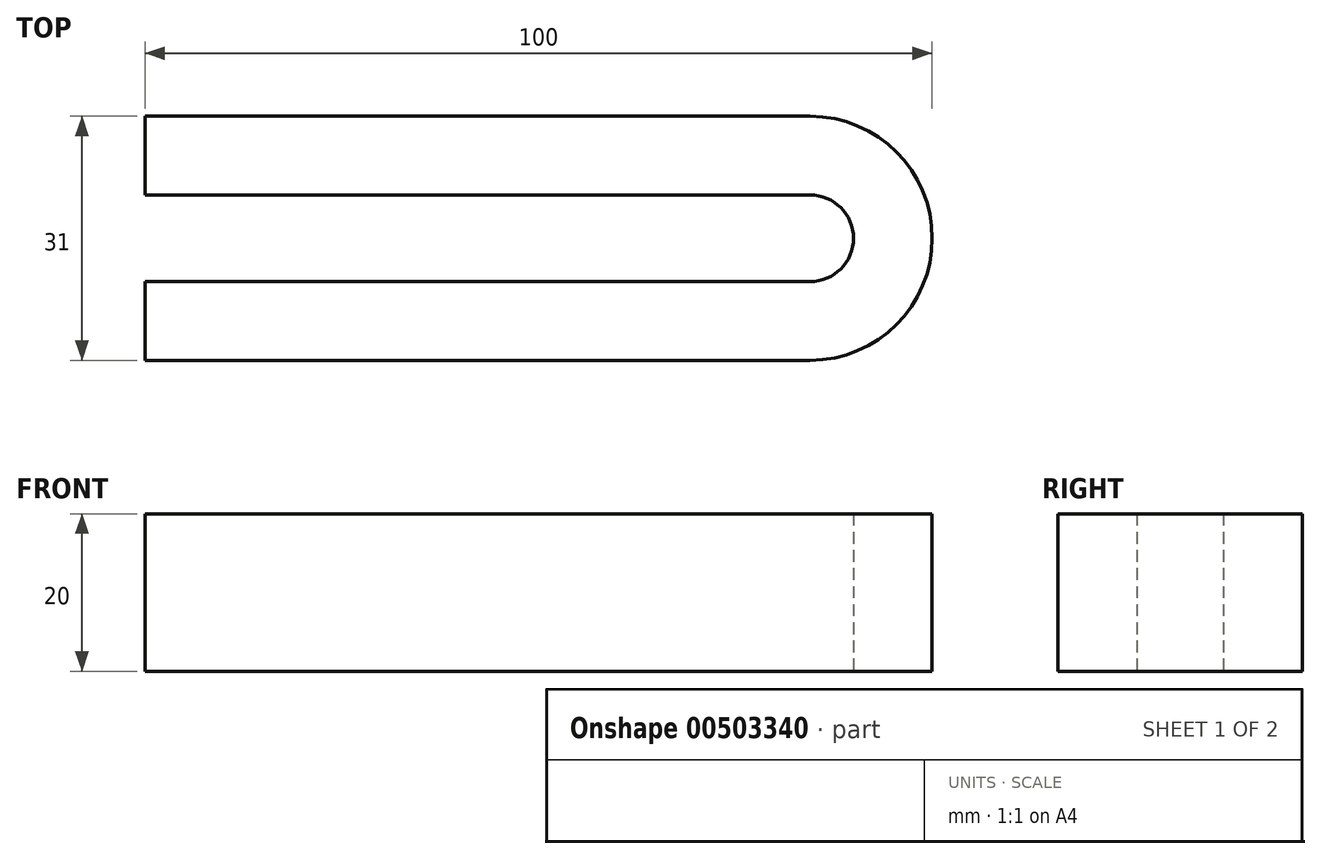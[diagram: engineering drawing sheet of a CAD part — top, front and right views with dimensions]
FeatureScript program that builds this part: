
annotation { "Feature Type Name" : "Feature", "Feature Type Description" : "" }
export const myFeature = defineFeature(function(context is Context, id is Id, definition is map)
    precondition{}
    {
        {
            var Q0;
            Q0=qCreatedBy(makeId("Top.planeOp"),FACE);
            var sketch = newSketch(context, id + "F0", { "sketchPlane" : qUnion([Q0])});
            skLineSegment(sketch, "E0.bottom", {"start": v(0, 0) * mm, "end": v(84.5, 0) * mm});
            skLineSegment(sketch, "E0.top", {"start": v(0, 31) * mm, "end": v(84.5, 31) * mm});
            skLineSegment(sketch, "E0.left", {"start": v(0, 0) * mm, "end": v(0, 31) * mm});
            skLineSegment(sketch, "E0.right", {"start": v(100, 15.5) * mm, "end": v(100, 15.5) * mm});
            skPoint(sketch, "E1.visualSharp", {"position": v(100, 0) * mm});
            skArc(sketch, "E1.filletArc", {"start": v(84.5, 0) * mm, "mid": v(95.46, 4.54) * mm, "end": v(100, 15.5) * mm});
            skPoint(sketch, "E2.visualSharp", {"position": v(100, 31) * mm});
            skArc(sketch, "E2.filletArc", {"start": v(100, 15.5) * mm, "mid": v(95.46, 26.46) * mm, "end": v(84.5, 31) * mm});
            skLineSegment(sketch, "E3.bottom", {"start": v(0, 10) * mm, "end": v(84.5, 10) * mm});
            skLineSegment(sketch, "E3.top", {"start": v(0, 21) * mm, "end": v(84.5, 21) * mm});
            skLineSegment(sketch, "E3.left", {"start": v(0, 10) * mm, "end": v(0, 21) * mm});
            skLineSegment(sketch, "E3.right", {"start": v(90, 15.5) * mm, "end": v(90, 15.5) * mm});
            skPoint(sketch, "E4.visualSharp", {"position": v(90, 21) * mm});
            skArc(sketch, "E4.filletArc", {"start": v(90, 15.5) * mm, "mid": v(88.39, 19.39) * mm, "end": v(84.5, 21) * mm});
            skPoint(sketch, "E5.visualSharp", {"position": v(90, 10) * mm});
            skArc(sketch, "E5.filletArc", {"start": v(84.5, 10) * mm, "mid": v(88.39, 11.61) * mm, "end": v(90, 15.5) * mm});
            skSolve(sketch);
        }
        {
            var Q0;
            {var subQ2=sQuery(id+"F0.wireOp",EDGE,"E0.bottom");Q0=makeQuery(id+"F0.imprint","IMPRINT",FACE,{"disambiguationData":[TD([[makeQuery(id+"F0.imprint","IMPRINT",EDGE,{"derivedFrom":subQ2}),1.0]])]});}
            extrude(context, id + "F1", {"entities" : qUnion([Q0]), "depth" : 20 * mm});
        }
    });
